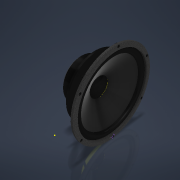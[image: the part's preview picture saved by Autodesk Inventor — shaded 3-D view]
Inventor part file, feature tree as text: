
AUTODESK INVENTOR PART (.ipt)
format: ipt  version: 2022 (Build 260153070, 153G)  size: 529,920 bytes
history: native  units: mm
features: sketch x6, hole x2, pattern_circular x2, other x1, revolve x1, extrude x1
ambient origin geometry x8: Origin, YZ Plane, XZ Plane, XY Plane, X Axis, Y Axis, Z Axis, Center Point
bodies: Body1 (feature_tree)
feature tree (13):
  other  "Твердое тело1"
  revolve  "Вращение1"
  sketch  "Эскиз2"
  sketch  "Эскиз3"
  hole  "Отверстие1"  [1 undecoded]
  pattern_circular  "Круговой массив1"  [2 undecoded]
  hole  "Отверстие2"  [1 undecoded]
  sketch  "Эскиз5"
  extrude  "Выдавливание1"  TaperAngle=360.0deg  [1 undecoded]
  pattern_circular  "Круговой массив2"  Count=6 Angle=360.0deg
  sketch  "Эскиз1"
  sketch  "Эскиз4"
  sketch  "Эскиз6"
note: 5 required parameter values undecoded (feature->parameter linkage not recoverable at this tier; creation-order binding heuristic only, values carry confidence <= 0.55)
